FCSTD DOCUMENT  (FreeCAD 1.0R39319 (Git))
Label: Assembly_PSU-Stack
License: All rights reserved
LicenseURL: https://en.wikipedia.org/wiki/All_rights_reserved
objects: App::FeaturePython×22, App::Link×11, Assembly::JointGroup×1, Assembly::AssemblyObject×1
EXTERNAL_REF file=../Part/Print/Stack_Module_PSU.FCStd obj=Part
EXTERNAL_REF file=../Part/Print/Ambient_LED_Screen.FCStd obj=Part
EXTERNAL_REF file=../Part/Print/LinePower_Cover.FCStd obj=Part
EXTERNAL_REF file=../Part/Print/Foot.FCStd obj=Part
EXTERNAL_REF file=../Part/Print/Spacer.FCStd obj=Part

FEATURE [App::Link] Stack_Module_PSU
  LinkedObject = -> <external ../Part/Print/Stack_Module_PSU.FCStd>#Part
FEATURE [App::FeaturePython] GroundedJoint  # Assembly grounded joint (typed FeaturePython)
  ObjectToGround = -> Stack_Module_PSU
FEATURE [App::Link] Ambient_LED_Screen
  LinkPlacement = pos=(-1.22e-14,-3,-62.5) rot=(0,0.707107,-0.707107;3.14159rad)
  LinkedObject = -> <external ../Part/Print/Ambient_LED_Screen.FCStd>#Part
  Placement = pos=(-1.22e-14,-3,-62.5) rot=(0,0.707107,-0.707107;3.14159rad)
FEATURE [App::FeaturePython] Joint  label="Distance"  # Assembly joint (typed FeaturePython)
  Activated = true
  AngleMax = 0
  AngleMin = 0
  Detach1 = false
  Detach2 = false
  Distance = 0
  Distance2 = 0
  EnableAngleMax = false
  EnableAngleMin = false
  EnableLengthMax = false
  EnableLengthMin = false
  JointType = 5 (Distance)
  LengthMax = 0
  LengthMin = 0
  Placement1 = pos=(5.02e-14,1.20274,-3.5e-15) rot=(0,1,0;3.14159rad)
  Placement2 = pos=(-3.81809,-3,-7.3136) rot=(1,0,0;1.5708rad)
  Reference1 = -> Assembly [Ambient_LED_Screen.Body.Face51,Ambient_LED_Screen.Body.Edge30]
  Reference2 = -> Assembly [Stack_Module_PSU.Body.Face1201,Stack_Module_PSU.Body.Edge768]
FEATURE [App::FeaturePython] Joint001  label="Cylindrical"  # Assembly joint (typed FeaturePython)
  Activated = true
  AngleMax = 0
  AngleMin = 0
  Detach1 = false
  Detach2 = false
  Distance = 0
  Distance2 = 0
  EnableAngleMax = false
  EnableAngleMin = false
  EnableLengthMax = false
  EnableLengthMin = false
  JointType = 2 (Cylindrical)
  LengthMax = 0
  LengthMin = 0
  Placement1 = pos=(60.5,3,0) rot=(1,0,0;3.14159rad)
  Placement2 = pos=(-60.5,1.29e-14,-65.5) rot=(0,0.707107,0.707107;3.14159rad)
  Reference1 = -> Assembly [Ambient_LED_Screen.Body.Face52,Ambient_LED_Screen.Body.Edge2]
  Reference2 = -> Assembly [Stack_Module_PSU.Body.Face1184,Stack_Module_PSU.Body.Edge3]
FEATURE [App::FeaturePython] Joint002  label="Cylindrical001"  # Assembly joint (typed FeaturePython)
  Activated = true
  AngleMax = 0
  AngleMin = 0
  Detach1 = false
  Detach2 = false
  Distance = 0
  Distance2 = 0
  EnableAngleMax = false
  EnableAngleMin = false
  EnableLengthMax = false
  EnableLengthMin = false
  JointType = 2 (Cylindrical)
  LengthMax = 0
  LengthMin = 0
  Placement1 = pos=(-60.5,3,-1.34e-14) rot=(0,0,1;3.14159rad)
  Placement2 = pos=(60.5,-1.5,-65.5) rot=(1,0,0;1.5708rad)
  Reference1 = -> Assembly [Ambient_LED_Screen.Body.Face54,Ambient_LED_Screen.Body.Edge2]
  Reference2 = -> Assembly [Stack_Module_PSU.Body.Face1185,Stack_Module_PSU.Body.Face1185]
FEATURE [App::Link] LinePower_Cover
  LinkPlacement = pos=(56,-4,67) rot=(0,-0.707107,0.707107;3.14159rad)
  LinkedObject = -> <external ../Part/Print/LinePower_Cover.FCStd>#Part
  Placement = pos=(56,-4,67) rot=(0,-0.707107,0.707107;3.14159rad)
FEATURE [App::FeaturePython] Joint003  label="Distance001"  # Assembly joint (typed FeaturePython)
  Activated = true
  AngleMax = 0
  AngleMin = 0
  Detach1 = false
  Detach2 = false
  Distance = 0
  Distance2 = 0
  EnableAngleMax = false
  EnableAngleMin = false
  EnableLengthMax = false
  EnableLengthMin = false
  JointType = 5 (Distance)
  LengthMax = 0
  LengthMin = 0
  Placement1 = pos=(42.2837,4.81718,4) rot=(0,0,1;0rad)
  Placement2 = pos=(12.8084,-8,63.1916) rot=(0.57735,0.57735,0.57735;4.18879rad)
  Reference1 = -> Assembly [LinePower_Cover.Body.Face19,LinePower_Cover.Body.Face19]
  Reference2 = -> Assembly [Stack_Module_PSU.Body.Face1235,Stack_Module_PSU.Body.Edge6]
FEATURE [App::FeaturePython] Joint004  label="Cylindrical002"  # Assembly joint (typed FeaturePython)
  Activated = true
  AngleMax = 0
  AngleMin = 0
  Detach1 = false
  Detach2 = false
  Distance = 0
  Distance2 = 0
  EnableAngleMax = false
  EnableAngleMin = false
  EnableLengthMax = false
  EnableLengthMin = false
  JointType = 2 (Cylindrical)
  LengthMax = 0
  LengthMin = 0
  Placement1 = pos=(43,4,5) rot=(0,0,1;0rad)
  Placement2 = pos=(13,-5.5,63) rot=(1,0,0;1.5708rad)
  Reference1 = -> Assembly [LinePower_Cover.Body.Face35,LinePower_Cover.Body.Face35]
  Reference2 = -> Assembly [Stack_Module_PSU.Body.Face1271,Stack_Module_PSU.Body.Face1271]
FEATURE [App::FeaturePython] Joint005  label="Cylindrical003"  # Assembly joint (typed FeaturePython)
  Activated = true
  AngleMax = 0
  AngleMin = 0
  Detach1 = false
  Detach2 = false
  Distance = 0
  Distance2 = 0
  EnableAngleMax = false
  EnableAngleMin = false
  EnableLengthMax = false
  EnableLengthMin = false
  JointType = 2 (Cylindrical)
  LengthMax = 0
  LengthMin = 0
  Placement1 = pos=(3,36,5) rot=(0,0,1;0rad)
  Placement2 = pos=(53,-5.5,31) rot=(1,0,0;1.5708rad)
  Reference1 = -> Assembly [LinePower_Cover.Body.Face36,LinePower_Cover.Body.Face36]
  Reference2 = -> Assembly [Stack_Module_PSU.Body.Face1265,Stack_Module_PSU.Body.Face1265]
FEATURE [App::Link] Foot
  LinkPlacement = pos=(-66.5,5,-53.5) rot=(0.57735,-0.57735,0.57735;2.0944rad)
  LinkedObject = -> <external ../Part/Print/Foot.FCStd>#Part
  Placement = pos=(-66.5,5,-53.5) rot=(0.57735,-0.57735,0.57735;2.0944rad)
FEATURE [App::Link] Foot001
  LinkPlacement = pos=(-63.5,5,62.5) rot=(0.57735,-0.57735,0.57735;2.0944rad)
  LinkedObject = -> <external ../Part/Print/Foot.FCStd>#Part
  Placement = pos=(-63.5,5,62.5) rot=(0.57735,-0.57735,0.57735;2.0944rad)
FEATURE [App::Link] Foot002
  LinkPlacement = pos=(66.5,5,-53.5) rot=(1,0,0;1.5708rad)
  LinkedObject = -> <external ../Part/Print/Foot.FCStd>#Part
  Placement = pos=(66.5,5,-53.5) rot=(1,0,0;1.5708rad)
FEATURE [App::Link] Foot003
  LinkPlacement = pos=(63.5,5,62.5) rot=(0.57735,-0.57735,0.57735;2.0944rad)
  LinkedObject = -> <external ../Part/Print/Foot.FCStd>#Part
  Placement = pos=(63.5,5,62.5) rot=(0.57735,-0.57735,0.57735;2.0944rad)
FEATURE [App::FeaturePython] Joint006  label="Cylindrical004"  # Assembly joint (typed FeaturePython)
  Activated = true
  AngleMax = 0
  AngleMin = 0
  Detach1 = false
  Detach2 = false
  Distance = 0
  Distance2 = 0
  EnableAngleMax = false
  EnableAngleMin = false
  EnableLengthMax = false
  EnableLengthMin = false
  JointType = 2 (Cylindrical)
  LengthMax = 0
  LengthMin = 0
  Placement1 = pos=(0,4e-16,2) rot=(1,0,0;3.14159rad)
  Placement2 = pos=(66.5,-2.5,-53.5) rot=(-1,0,0;1.5708rad)
  Reference1 = -> Assembly [Foot002.Body.Face12,Foot002.Body.Face12]
  Reference2 = -> Assembly [Stack_Module_PSU.Body.Face83,Stack_Module_PSU.Body.Face83]
FEATURE [App::FeaturePython] Joint007  label="Distance002"  # Assembly joint (typed FeaturePython)
  Activated = true
  AngleMax = 0
  AngleMin = 0
  Detach1 = false
  Detach2 = false
  Distance = 0
  Distance2 = 0
  EnableAngleMax = false
  EnableAngleMin = false
  EnableLengthMax = false
  EnableLengthMin = false
  JointType = 5 (Distance)
  LengthMax = 0
  LengthMin = 0
  Placement1 = pos=(9e-16,2.4e-15,5) rot=(0,0,1;3.14159rad)
  Placement2 = pos=(1.08804,3.9e-15,3.01175) rot=(-0.57735,0.57735,0.57735;2.0944rad)
  Reference1 = -> Assembly [Foot002.Body.Face3,Foot002.Body.Face3]
  Reference2 = -> Assembly [Stack_Module_PSU.Body.Face7,Stack_Module_PSU.Body.Vertex102]
FEATURE [App::FeaturePython] Joint008  label="Distance003"  # Assembly joint (typed FeaturePython)
  Activated = true
  AngleMax = 0
  AngleMin = 0
  Detach1 = false
  Detach2 = false
  Distance = 0
  Distance2 = 0
  EnableAngleMax = false
  EnableAngleMin = false
  EnableLengthMax = false
  EnableLengthMin = false
  JointType = 5 (Distance)
  LengthMax = 0
  LengthMin = 0
  Placement1 = pos=(9e-16,2.4e-15,5) rot=(0,0,1;3.14159rad)
  Placement2 = pos=(1.08804,3.9e-15,3.01175) rot=(-0.57735,0.57735,0.57735;2.0944rad)
  Reference1 = -> Assembly [Foot003.Body.Face3,Foot003.Body.Face3]
  Reference2 = -> Assembly [Stack_Module_PSU.Body.Face7,Stack_Module_PSU.Body.Vertex92]
FEATURE [App::FeaturePython] Joint009  label="Cylindrical005"  # Assembly joint (typed FeaturePython)
  Activated = true
  AngleMax = 0
  AngleMin = 0
  Detach1 = false
  Detach2 = false
  Distance = 0
  Distance2 = 0
  EnableAngleMax = false
  EnableAngleMin = false
  EnableLengthMax = false
  EnableLengthMin = false
  JointType = 2 (Cylindrical)
  LengthMax = 0
  LengthMin = 0
  Placement1 = pos=(0,4e-16,2) rot=(1,0,0;3.14159rad)
  Placement2 = pos=(63.5,-2.5,62.5) rot=(-1,0,0;1.5708rad)
  Reference1 = -> Assembly [Foot003.Body.Face12,Foot003.Body.Face12]
  Reference2 = -> Assembly [Stack_Module_PSU.Body.Face82,Stack_Module_PSU.Body.Face82]
FEATURE [App::FeaturePython] Joint010  label="Distance004"  # Assembly joint (typed FeaturePython)
  Activated = true
  AngleMax = 0
  AngleMin = 0
  Detach1 = false
  Detach2 = false
  Distance = 0
  Distance2 = 0
  EnableAngleMax = false
  EnableAngleMin = false
  EnableLengthMax = false
  EnableLengthMin = false
  JointType = 5 (Distance)
  LengthMax = 0
  LengthMin = 0
  Placement1 = pos=(9e-16,2.4e-15,5) rot=(0,0,1;3.14159rad)
  Placement2 = pos=(1.08804,3.9e-15,3.01175) rot=(-0.57735,0.57735,0.57735;2.0944rad)
  Reference1 = -> Assembly [Foot001.Body.Face3,Foot001.Body.Face3]
  Reference2 = -> Assembly [Stack_Module_PSU.Body.Face7,Stack_Module_PSU.Body.Vertex89]
FEATURE [App::FeaturePython] Joint011  label="Cylindrical006"  # Assembly joint (typed FeaturePython)
  Activated = true
  AngleMax = 0
  AngleMin = 0
  Detach1 = false
  Detach2 = false
  Distance = 0
  Distance2 = 0
  EnableAngleMax = false
  EnableAngleMin = false
  EnableLengthMax = false
  EnableLengthMin = false
  JointType = 2 (Cylindrical)
  LengthMax = 0
  LengthMin = 0
  Placement1 = pos=(0,4e-16,2) rot=(1,0,0;3.14159rad)
  Placement2 = pos=(-63.5,-2.5,62.5) rot=(0,0.707107,-0.707107;3.14159rad)
  Reference1 = -> Assembly [Foot001.Body.Face12,Foot001.Body.Face12]
  Reference2 = -> Assembly [Stack_Module_PSU.Body.Face80,Stack_Module_PSU.Body.Face80]
FEATURE [App::FeaturePython] Joint012  label="Distance005"  # Assembly joint (typed FeaturePython)
  Activated = true
  AngleMax = 0
  AngleMin = 0
  Detach1 = false
  Detach2 = false
  Distance = 0
  Distance2 = 0
  EnableAngleMax = false
  EnableAngleMin = false
  EnableLengthMax = false
  EnableLengthMin = false
  JointType = 5 (Distance)
  LengthMax = 0
  LengthMin = 0
  Placement1 = pos=(9e-16,2.4e-15,5) rot=(0,0,1;3.14159rad)
  Placement2 = pos=(1.08804,3.9e-15,3.01175) rot=(-0.57735,0.57735,0.57735;2.0944rad)
  Reference1 = -> Assembly [Foot.Body.Face3,Foot.Body.Face3]
  Reference2 = -> Assembly [Stack_Module_PSU.Body.Face7,Stack_Module_PSU.Body.Edge11]
FEATURE [App::FeaturePython] Joint013  label="Cylindrical007"  # Assembly joint (typed FeaturePython)
  Activated = true
  AngleMax = 0
  AngleMin = 0
  Detach1 = false
  Detach2 = false
  Distance = 0
  Distance2 = 0
  EnableAngleMax = false
  EnableAngleMin = false
  EnableLengthMax = false
  EnableLengthMin = false
  JointType = 2 (Cylindrical)
  LengthMax = 0
  LengthMin = 0
  Placement1 = pos=(0,4e-16,2) rot=(1,0,0;3.14159rad)
  Placement2 = pos=(-66.5,-2.5,-53.5) rot=(0,0.707107,-0.707107;3.14159rad)
  Reference1 = -> Assembly [Foot.Body.Face12,Foot.Body.Face12]
  Reference2 = -> Assembly [Stack_Module_PSU.Body.Face81,Stack_Module_PSU.Body.Face81]
FEATURE [App::Link] Spacer
  LinkPlacement = pos=(66.5,-35.25,-53.5) rot=(-0.57735,0.57735,-0.57735;4.18879rad)
  LinkedObject = -> <external ../Part/Print/Spacer.FCStd>#Part
  Placement = pos=(66.5,-35.25,-53.5) rot=(-0.57735,0.57735,-0.57735;4.18879rad)
FEATURE [App::Link] Spacer001
  LinkPlacement = pos=(63.5,-35.25,62.5) rot=(-0.57735,0.57735,-0.57735;4.18879rad)
  LinkedObject = -> <external ../Part/Print/Spacer.FCStd>#Part
  Placement = pos=(63.5,-35.25,62.5) rot=(-0.57735,0.57735,-0.57735;4.18879rad)
FEATURE [App::Link] Spacer002
  LinkPlacement = pos=(-66.5,-35.25,-53.5) rot=(-0.57735,0.57735,-0.57735;4.18879rad)
  LinkedObject = -> <external ../Part/Print/Spacer.FCStd>#Part
  Placement = pos=(-66.5,-35.25,-53.5) rot=(-0.57735,0.57735,-0.57735;4.18879rad)
FEATURE [App::Link] Spacer003
  LinkPlacement = pos=(-63.5,-35.25,62.5) rot=(0.57735,-0.57735,0.57735;2.0944rad)
  LinkedObject = -> <external ../Part/Print/Spacer.FCStd>#Part
  Placement = pos=(-63.5,-35.25,62.5) rot=(0.57735,-0.57735,0.57735;2.0944rad)
FEATURE [App::FeaturePython] Joint014  label="Distance006"  # Assembly joint (typed FeaturePython)
  Activated = true
  AngleMax = 0
  AngleMin = 0
  Detach1 = false
  Detach2 = false
  Distance = 0
  Distance2 = 0
  EnableAngleMax = false
  EnableAngleMin = false
  EnableLengthMax = false
  EnableLengthMin = false
  JointType = 5 (Distance)
  LengthMax = 0
  LengthMin = 0
  Placement1 = pos=(-3.1e-15,-9e-16,0) rot=(0,0,1;0rad)
  Placement2 = pos=(66.5,-35.25,-53.5) rot=(0.57735,0.57735,0.57735;4.18879rad)
  Reference1 = -> Assembly [Spacer.Body.Face4,Spacer.Body.Face4]
  Reference2 = -> Assembly [Stack_Module_PSU.Body.Face1241,Stack_Module_PSU.Body.Face1241]
FEATURE [App::FeaturePython] Joint015  label="Cylindrical008"  # Assembly joint (typed FeaturePython)
  Activated = true
  AngleMax = 0
  AngleMin = 0
  Detach1 = false
  Detach2 = false
  Distance = 0
  Distance2 = 0
  EnableAngleMax = false
  EnableAngleMin = false
  EnableLengthMax = false
  EnableLengthMin = false
  JointType = 2 (Cylindrical)
  LengthMax = 0
  LengthMin = 0
  Placement1 = pos=(0,0,3.5) rot=(0,0,1;0rad)
  Placement2 = pos=(66.5,-37.75,-53.5) rot=(1,0,0;1.5708rad)
  Reference1 = -> Assembly [Spacer.Body.Face1,Spacer.Body.Face1]
  Reference2 = -> Assembly [Stack_Module_PSU.Body.Face71,Stack_Module_PSU.Body.Face71]
FEATURE [App::FeaturePython] Joint016  label="Distance007"  # Assembly joint (typed FeaturePython)
  Activated = true
  AngleMax = 0
  AngleMin = 0
  Detach1 = false
  Detach2 = false
  Distance = 0
  Distance2 = 0
  EnableAngleMax = false
  EnableAngleMin = false
  EnableLengthMax = false
  EnableLengthMin = false
  JointType = 5 (Distance)
  LengthMax = 0
  LengthMin = 0
  Placement1 = pos=(-3.1e-15,-9e-16,0) rot=(0,0,1;0rad)
  Placement2 = pos=(63.5,-35.25,62.5) rot=(0.57735,0.57735,0.57735;4.18879rad)
  Reference1 = -> Assembly [Spacer001.Body.Face4,Spacer001.Body.Face4]
  Reference2 = -> Assembly [Stack_Module_PSU.Body.Face1240,Stack_Module_PSU.Body.Edge2]
FEATURE [App::FeaturePython] Joint017  label="Distance008"  # Assembly joint (typed FeaturePython)
  Activated = true
  AngleMax = 0
  AngleMin = 0
  Detach1 = false
  Detach2 = false
  Distance = 0
  Distance2 = 0
  EnableAngleMax = false
  EnableAngleMin = false
  EnableLengthMax = false
  EnableLengthMin = false
  JointType = 5 (Distance)
  LengthMax = 0
  LengthMin = 0
  Placement1 = pos=(-3.1e-15,-9e-16,0) rot=(0,0,1;0rad)
  Placement2 = pos=(-66.5,-35.25,-53.5) rot=(0.57735,-0.57735,0.57735;2.0944rad)
  Reference1 = -> Assembly [Spacer002.Body.Face4,Spacer002.Body.Vertex5]
  Reference2 = -> Assembly [Stack_Module_PSU.Body.Face1239,Stack_Module_PSU.Body.Vertex2511]
FEATURE [App::FeaturePython] Joint018  label="Cylindrical009"  # Assembly joint (typed FeaturePython)
  Activated = true
  AngleMax = 0
  AngleMin = 0
  Detach1 = false
  Detach2 = false
  Distance = 0
  Distance2 = 0
  EnableAngleMax = false
  EnableAngleMin = false
  EnableLengthMax = false
  EnableLengthMin = false
  JointType = 2 (Cylindrical)
  LengthMax = 0
  LengthMin = 0
  Placement1 = pos=(0,0,3.5) rot=(0,0,1;0rad)
  Placement2 = pos=(-66.5,-37.75,-53.5) rot=(0,0.707107,0.707107;3.14159rad)
  Reference1 = -> Assembly [Spacer002.Body.Face1,Spacer002.Body.Face1]
  Reference2 = -> Assembly [Stack_Module_PSU.Body.Face69,Stack_Module_PSU.Body.Face69]
FEATURE [App::FeaturePython] Joint019  label="Distance009"  # Assembly joint (typed FeaturePython)
  Activated = true
  AngleMax = 0
  AngleMin = 0
  Detach1 = false
  Detach2 = false
  Distance = 0
  Distance2 = 0
  EnableAngleMax = false
  EnableAngleMin = false
  EnableLengthMax = false
  EnableLengthMin = false
  JointType = 5 (Distance)
  LengthMax = 0
  LengthMin = 0
  Placement1 = pos=(-3.1e-15,-9e-16,0) rot=(0,0,1;0rad)
  Placement2 = pos=(-63.5,-35.25,62.5) rot=(0.57735,-0.57735,0.57735;2.0944rad)
  Reference1 = -> Assembly [Spacer003.Body.Face4,Spacer003.Body.Vertex5]
  Reference2 = -> Assembly [Stack_Module_PSU.Body.Face1238,Stack_Module_PSU.Body.Vertex2510]
FEATURE [App::FeaturePython] Joint020  label="Cylindrical010"  # Assembly joint (typed FeaturePython)
  Activated = true
  AngleMax = 0
  AngleMin = 0
  Detach1 = false
  Detach2 = false
  Distance = 0
  Distance2 = 0
  EnableAngleMax = false
  EnableAngleMin = false
  EnableLengthMax = false
  EnableLengthMin = false
  JointType = 2 (Cylindrical)
  LengthMax = 0
  LengthMin = 0
  Placement1 = pos=(0,0,3.5) rot=(0,0,1;0rad)
  Placement2 = pos=(-63.5,-37.75,62.5) rot=(0,0.707107,0.707107;3.14159rad)
  Reference1 = -> Assembly [Spacer003.Body.Face1,Spacer003.Body.Face1]
  Reference2 = -> Assembly [Stack_Module_PSU.Body.Face68,Stack_Module_PSU.Body.Face68]
FEATURE [Assembly::JointGroup] Joints
  Group = -> [GroundedJoint,Joint,Joint001,Joint002,Joint003,Joint004,Joint005,Joint006,Joint007,Joint008,Joint009,Joint010,Joint011,Joint012,Joint013,Joint014,Joint015,Joint016,Joint017,Joint018,Joint019,Joint020]
FEATURE [Assembly::AssemblyObject] Assembly  label="Assembly_PSU-Stack"
  Group = -> [Joints,Stack_Module_PSU,GroundedJoint,Ambient_LED_Screen,Joint,Joint001,Joint002,LinePower_Cover,Joint003,Joint004,Joint005,Foot,Foot001,Foot002,Foot003,Joint006,Joint007,Joint008,Joint009,Joint010,Joint011,Joint012,Joint013,Spacer,Spacer001,Spacer002,Spacer003,Joint014,Joint015,Joint016,Joint017,Joint018,Joint019,Joint020]
  Origin = -> Origin
  Type = Assembly

RESOLVED EXTERNAL PARTS (link-assembly join: the EXTERNAL_REF files above that resolve inside this repo's crawl, each included once):
---- part ../Part/Print/Ambient_LED_Screen.FCStd = doc fcstd_3e985b0e07c3 ----
FCSTD DOCUMENT  (FreeCAD 1.0R39319 (Git))
Label: Ambient_LED_Screen
License: All rights reserved
LicenseURL: https://en.wikipedia.org/wiki/All_rights_reserved
objects: Sketcher::SketchObject×7, PartDesign::Pocket×5, PartDesign::Pad×2, PartDesign::Chamfer×1, PartDesign::Mirrored×1, PartDesign::Body×1, PartDesign::CoordinateSystem×1, App::Part×1
note: 42 computed .brp shape members not serialized (recipe doc carries the construction recipe); baked Part::Feature solids carry a one-line shape summary decoded from their .brp

FEATURE [Sketcher::SketchObject] Sketch
  ArcFitTolerance = 1e-06
  AttachmentSupport = -> [XY_Plane001]
  FullyConstrained = true
  MakeInternals = false
  MapMode = 5
  sketch-geometry (20):
    g0: LineSegment StartX=52.3059 StartY=0 StartZ=0 EndX=60.5 EndY=0 EndZ=0
    g1: ArcOfCircle CenterX=60.5 CenterY=3 CenterZ=0 NormalX=0 NormalY=0 NormalZ=1 AngleXU=0 Radius=3 StartAngle=4.71239 EndAngle=8.29889
    g2: LineSegment StartX=59.2089 StartY=5.70795 StartZ=0 EndX=48.6478 EndY=0.672534 EndZ=0
    g3: ArcOfCircle CenterX=0 CenterY=4.259 CenterZ=0 NormalX=0 NormalY=0 NormalZ=1 AngleXU=0 Radius=7 StartAngle=4.71239 EndAngle=5.61581
    g4: ArcOfCircle CenterX=0 CenterY=4.259 CenterZ=0 NormalX=0 NormalY=0 NormalZ=1 AngleXU=0 Radius=5.5 StartAngle=4.71239 EndAngle=5.61581
    g5: LineSegment StartX=-1.3e-15 StartY=-2.741 StartZ=0 EndX=-1.3e-15 EndY=-1.241 EndZ=0
    g6: ArcOfCircle CenterX=10.9963 CenterY=-4.40596 CenterZ=0 NormalX=0 NormalY=0 NormalZ=1 AngleXU=0 Radius=7 StartAngle=0.667374 EndAngle=2.47422
    g7: ArcOfCircle CenterX=10.9963 CenterY=-4.40596 CenterZ=0 NormalX=0 NormalY=0 NormalZ=1 AngleXU=0 Radius=8.5 StartAngle=0.667374 EndAngle=2.47422
    g8: ArcOfCircle CenterX=21.9926 CenterY=4.259 CenterZ=0 NormalX=0 NormalY=0 NormalZ=1 AngleXU=0 Radius=5.5 StartAngle=3.80897 EndAngle=5.61581
    g9: ArcOfCircle CenterX=21.9926 CenterY=4.259 CenterZ=0 NormalX=0 NormalY=0 NormalZ=1 AngleXU=0 Radius=7 StartAngle=3.80897 EndAngle=5.61581
    g10: ArcOfCircle CenterX=32.9889 CenterY=-4.40596 CenterZ=0 NormalX=0 NormalY=0 NormalZ=1 AngleXU=0 Radius=8.5 StartAngle=0.667374 EndAngle=2.47422
    g11: ArcOfCircle CenterX=32.9889 CenterY=-4.40596 CenterZ=0 NormalX=0 NormalY=0 NormalZ=1 AngleXU=0 Radius=7 StartAngle=0.667374 EndAngle=2.47422
    g12: ArcOfCircle CenterX=43.9852 CenterY=4.259 CenterZ=0 NormalX=0 NormalY=0 NormalZ=1 AngleXU=0 Radius=7 StartAngle=3.80897 EndAngle=5.34883
    g13: ArcOfCircle CenterX=43.9852 CenterY=4.259 CenterZ=0 NormalX=0 NormalY=0 NormalZ=1 AngleXU=0 Radius=5.5 StartAngle=3.80897 EndAngle=5.34883
    g14: ArcOfCircle CenterX=52.3059 CenterY=-7 CenterZ=0 NormalX=0 NormalY=0 NormalZ=1 AngleXU=0 Radius=8.5 StartAngle=2.0157 EndAngle=2.20724
    g15: ArcOfCircle CenterX=52.3059 CenterY=-7 CenterZ=0 NormalX=0 NormalY=0 NormalZ=1 AngleXU=0 Radius=7 StartAngle=1.5708 EndAngle=2.20724
    g16: GeomPoint [constr] X=66 Y=10 Z=0
    g17: LineSegment [constr] StartX=48.1455 StartY=-1.3705 StartZ=0 EndX=50 EndY=2e-16 EndZ=0
    g18: LineSegment [constr] StartX=10.9963 StartY=-4.40596 StartZ=0 EndX=32.9889 EndY=-4.40596 EndZ=0
    g19: LineSegment [constr] StartX=0 StartY=4.259 StartZ=0 EndX=43.9852 EndY=4.259 EndZ=0
  constraints (49):
    c: PointOnObject(g0,g-1)
    c: PointOnObject(g0,g-1)
    c: Tangent(g0,g1) = -1.5708
    c: Tangent(g1,g2) = -1.5708
    c: Coincident(g5,g3)
    c: Coincident(g5,g4)
    c: Vertical(g5)
    c: Coincident(g4,g3)
    c: PointOnObject(g3,g-2)
    c: Tangent(g6,g3) = 1.5708
    c: Tangent(g7,g4) = 1.5708
    c: Coincident(g6,g7)
    c: Radius(g6) = 7
    c: Distance(g5,g5) = 1.5
    c: Tangent(g8,g7) = 1.5708
    c: Tangent(g9,g6) = 1.5708
    c: Coincident(g9,g8)
    c: PointOnObject(g3,g-2)
    c: Tangent(g10,g8) = 1.5708
    c: Tangent(g11,g9) = 1.5708
    c: Coincident(g11,g10)
    c: Tangent(g12,g11) = 1.5708
    c: Tangent(g13,g10) = 1.5708
    c: Coincident(g12,g13)
    c: Tangent(g14,g13) = 1.5708
    c: Tangent(g14,g2) = -1.5708
    c: Tangent(g15,g0) = 1.5708
    c: Radius(g9) = 7
    c: Radius(g12) = 7
    c: Coincident(g15,g14)
    c: DistanceX(g-1,g16) = 66
    c: Distance(g16,g-1) = 10
    c: Radius(g1) = 3
    c: Distance(g1,g-2) = 60.5
    c: Tangent(g15,g12) = 1.5708
    c: Tangent(g12,g17) = -1.5708
    c: Radius(g3) = 7
    c: Radius(g11) = 7
    c: Radius(g15) = 7
    c: PointOnObject(g17,g-1)
    c: DistanceX(g-1,g17) = 50
    c: Coincident(g18,g6)
    c: Coincident(g18,g10)
    c: Coincident(g19,g3)
    c: Coincident(g19,g12)
    c: Horizontal(g19)
    c: PointOnObject(g8,g19)
    c: Horizontal(g18)
    c: Distance(g-1,g19) = 4.259
FEATURE [PartDesign::Pad] Pad
  Direction = (0,0,1)
  Length = 34.25
  Length2 = 10
  Profile = -> Sketch
  ReferenceAxis = -> Sketch [N_Axis]
  Refine = true
  Suppressed = false
  Type = 0
FEATURE [Sketcher::SketchObject] Sketch001
  ArcFitTolerance = 1e-06
  AttachmentSupport = -> [Pad]
  ExternalGeometry = -> [Pad]
  FullyConstrained = true
  MakeInternals = false
  MapMode = 5
  Placement = pos=(0,0,0) rot=(1,0,0;3.14159rad)
  sketch-geometry (1):
    g0: Circle CenterX=60.5 CenterY=-3 CenterZ=0 NormalX=0 NormalY=0 NormalZ=1 AngleXU=0 Radius=1.25
  constraints (2):
    c: Coincident(g0,g-3)
    c: Diameter(g0) = 2.5
FEATURE [PartDesign::Pocket] Pocket
  BaseFeature = -> Pad
  Direction = (0,0,1)
  Length = 10
  Length2 = 5
  Profile = -> Sketch001
  ReferenceAxis = -> Sketch001 [N_Axis]
  Refine = true
  Suppressed = false
  Type = 0
FEATURE [Sketcher::SketchObject] Sketch002
  ArcFitTolerance = 1e-06
  AttachmentSupport = -> [Pocket]
  FullyConstrained = true
  MakeInternals = false
  MapMode = 5
  Placement = pos=(0,0,34.25) rot=(0,0,1;0rad)
  sketch-geometry (4):
    g0: LineSegment StartX=0 StartY=7.59 StartZ=0 EndX=0 EndY=-5.3 EndZ=0
    g1: LineSegment StartX=0 StartY=-5.3 StartZ=0 EndX=70.5 EndY=-5.3 EndZ=0
    g2: LineSegment StartX=70.5 StartY=-5.3 StartZ=0 EndX=70.5 EndY=7.59 EndZ=0
    g3: LineSegment StartX=70.5 StartY=7.59 StartZ=0 EndX=0 EndY=7.59 EndZ=0
  constraints (12):
    c: Coincident(g0,g1)
    c: Coincident(g1,g2)
    c: Coincident(g2,g3)
    c: Coincident(g3,g0)
    c: Vertical(g0)
    c: Vertical(g2)
    c: Horizontal(g1)
    c: Horizontal(g3)
    c: PointOnObject(g0,g-2)
    c: Distance(g2,g0) = 70.5
    c: Distance(g3,g1) = 12.89
    c: Distance(g1,g-1) = 5.3
FEATURE [PartDesign::Pad] Pad001
  BaseFeature = -> Pocket
  Direction = (0,0,1)
  Length = 3
  Length2 = 10
  Profile = -> Sketch002
  ReferenceAxis = -> Sketch002 [N_Axis]
  Refine = true
  Suppressed = false
  Type = 0
FEATURE [Sketcher::SketchObject] Sketch003
  ArcFitTolerance = 1e-06
  AttachmentSupport = -> [Pad001]
  ExternalGeometry = -> [Pad001]
  FullyConstrained = true
  MakeInternals = false
  MapMode = 5
  Placement = pos=(0,0,37.25) rot=(0,0,1;0rad)
  sketch-geometry (4):
    g0: LineSegment StartX=70.5 StartY=-2.5 StartZ=0 EndX=55.5 EndY=-2.5 EndZ=0
    g1: LineSegment StartX=55.5 StartY=-2.5 StartZ=0 EndX=55.5 EndY=-5.3 EndZ=0
    g2: LineSegment StartX=55.5 StartY=-5.3 StartZ=0 EndX=70.5 EndY=-5.3 EndZ=0
    g3: LineSegment StartX=70.5 StartY=-5.3 StartZ=0 EndX=70.5 EndY=-2.5 EndZ=0
  constraints (12):
    c: Coincident(g0,g1)
    c: Coincident(g1,g2)
    c: Coincident(g2,g3)
    c: Coincident(g3,g0)
    c: Horizontal(g0)
    c: Horizontal(g2)
    c: Vertical(g1)
    c: Vertical(g3)
    c: PointOnObject(g0,g-3)
    c: PointOnObject(g1,g-4)
    c: Distance(g3,g1) = 15
    c: Distance(g2,g0) = 2.8
FEATURE [PartDesign::Pocket] Pocket001
  BaseFeature = -> Pad001
  Direction = (0,0,-1)
  Length = 5
  Length2 = 5
  Profile = -> Sketch003
  ReferenceAxis = -> Sketch003 [N_Axis]
  Refine = true
  Suppressed = false
  Type = 1
FEATURE [Sketcher::SketchObject] Sketch004
  ArcFitTolerance = 1e-06
  AttachmentSupport = -> [Pocket001]
  ExternalGeometry = -> [Pocket001]
  FullyConstrained = true
  MakeInternals = false
  MapMode = 5
  Placement = pos=(0,0,37.25) rot=(0,0,1;0rad)
  sketch-geometry (4):
    g0: LineSegment StartX=65.5 StartY=7.59 StartZ=0 EndX=65.5 EndY=4.09 EndZ=0
    g1: LineSegment StartX=65.5 StartY=4.09 StartZ=0 EndX=70.5 EndY=4.09 EndZ=0
    g2: LineSegment StartX=70.5 StartY=4.09 StartZ=0 EndX=70.5 EndY=7.59 EndZ=0
    g3: LineSegment StartX=70.5 StartY=7.59 StartZ=0 EndX=65.5 EndY=7.59 EndZ=0
  constraints (12):
    c: Coincident(g0,g1)
    c: Coincident(g1,g2)
    c: Coincident(g2,g3)
    c: Coincident(g3,g0)
    c: Vertical(g0)
    c: Vertical(g2)
    c: Horizontal(g1)
    c: Horizontal(g3)
    c: PointOnObject(g0,g-4)
    c: Distance(g2,g0) = 5
    c: Distance(g1,g3) = 3.5
    c: PointOnObject(g1,g-3)
FEATURE [PartDesign::Pocket] Pocket002
  BaseFeature = -> Pocket001
  Direction = (0,0,-1)
  Length = 5
  Length2 = 5
  Profile = -> Sketch004
  ReferenceAxis = -> Sketch004 [N_Axis]
  Refine = true
  Suppressed = false
  Type = 1
FEATURE [Sketcher::SketchObject] Sketch005
  ArcFitTolerance = 1e-06
  AttachmentSupport = -> [Pocket002]
  ExternalGeometry = -> [Pocket002]
  FullyConstrained = true
  MakeInternals = false
  MapMode = 5
  Placement = pos=(0,0,37.25) rot=(0,0,1;0rad)
  sketch-geometry (1):
    g0: Circle CenterX=68 CenterY=1 CenterZ=0 NormalX=0 NormalY=0 NormalZ=1 AngleXU=0 Radius=1.5
  constraints (3):
    c: Distance(g0,g-2) = 68
    c: Distance(g0,g-3) = 3.5
    c: Diameter(g0) = 3
FEATURE [PartDesign::Pocket] Pocket003
  BaseFeature = -> Pocket002
  Direction = (0,0,-1)
  Length = 5
  Length2 = 5
  Profile = -> Sketch005
  ReferenceAxis = -> Sketch005 [N_Axis]
  Refine = true
  Suppressed = false
  Type = 1
FEATURE [Sketcher::SketchObject] Sketch006
  ArcFitTolerance = 1e-06
  AttachmentSupport = -> [Pocket003]
  ExternalGeometry = -> [Pocket003]
  FullyConstrained = true
  MakeInternals = false
  MapMode = 5
  Placement = pos=(0,0,37.25) rot=(0,0,1;0rad)
  sketch-geometry (2):
    g0: Circle CenterX=65.5 CenterY=4.09 CenterZ=0 NormalX=0 NormalY=0 NormalZ=1 AngleXU=0 Radius=0.5
    g1: Circle CenterX=55.5 CenterY=-2.5 CenterZ=0 NormalX=0 NormalY=0 NormalZ=1 AngleXU=0 Radius=0.5
  constraints (4):
    c: Coincident(g0,g-3)
    c: Coincident(g1,g-4)
    c: Diameter(g0) = 1
    c: Diameter(g1) = 1
FEATURE [PartDesign::Pocket] Pocket004
  BaseFeature = -> Pocket003
  Direction = (0,0,-1)
  Length = 5
  Length2 = 5
  Profile = -> Sketch006
  ReferenceAxis = -> Sketch006 [N_Axis]
  Refine = true
  Suppressed = false
  Type = 1
FEATURE [PartDesign::Chamfer] Chamfer
  Angle = 45
  Base = -> Pocket004 [Edge81,Edge68]
  BaseFeature = -> Pocket004
  ChamferType = 0
  FlipDirection = false
  Refine = true
  Size = 0.5
  Size2 = 1
  SupportTransform = false
  Suppressed = false
  UseAllEdges = false
FEATURE [PartDesign::Mirrored] Mirrored
  BaseFeature = -> Chamfer
  MirrorPlane = -> YZ_Plane001
  Refine = true
  Suppressed = false
  TransformMode = 1
FEATURE [PartDesign::Body] Body  label="Ambient_LED_Screen001"
  AllowCompound = false
  Group = -> [Sketch,Pad,Sketch001,Pocket,Sketch002,Pad001,Sketch003,Pocket001,Sketch004,Pocket002,Sketch005,Pocket003,Sketch006,Pocket004,Chamfer,Mirrored]
  Origin = -> Origin001
  Tip = -> Mirrored
FEATURE [PartDesign::CoordinateSystem] stack_att
  AttacherType = Attacher::AttachEngine3D
  AttachmentSupport = -> [Mirrored]
  MapMode = 11
  Placement = pos=(60.5,3,0) rot=(0.707107,-0.707107,0;3.14159rad)
FEATURE [App::Part] Part  label="Ambient_LED_Screen"
  Group = -> [Body,stack_att]
  Origin = -> Origin
---- part ../Part/Print/Foot.FCStd = doc fcstd_07f4133909bb ----
FCSTD DOCUMENT  (FreeCAD 1.0R39319 (Git))
Label: Foot
License: All rights reserved
LicenseURL: https://en.wikipedia.org/wiki/All_rights_reserved
objects: Sketcher::SketchObject×3, PartDesign::Pocket×2, PartDesign::CoordinateSystem×2, PartDesign::Revolution×1, PartDesign::Fillet×1, PartDesign::Chamfer×1, PartDesign::Body×1, App::Part×1
note: 24 computed .brp shape members not serialized (recipe doc carries the construction recipe); baked Part::Feature solids carry a one-line shape summary decoded from their .brp

FEATURE [Sketcher::SketchObject] Sketch
  ArcFitTolerance = 1e-06
  AttachmentSupport = -> [XZ_Plane001]
  FullyConstrained = true
  MakeInternals = false
  MapMode = 5
  Placement = pos=(0,0,0) rot=(1,0,0;1.5708rad)
  sketch-geometry (6):
    g0: LineSegment StartX=0 StartY=0 StartZ=0 EndX=0 EndY=9 EndZ=0
    g1: LineSegment StartX=0 StartY=9 StartZ=0 EndX=5.5 EndY=9 EndZ=0
    g2: LineSegment StartX=5.5 StartY=9 StartZ=0 EndX=5.5 EndY=5 EndZ=0
    g3: LineSegment StartX=5.5 StartY=5 StartZ=0 EndX=7.5 EndY=5 EndZ=0
    g4: LineSegment StartX=7.5 StartY=5 StartZ=0 EndX=7.5 EndY=0 EndZ=0
    g5: LineSegment StartX=7.5 StartY=0 StartZ=0 EndX=0 EndY=0 EndZ=0
  constraints (17):
    c: Coincident(g-1,g0)
    c: PointOnObject(g0,g-2)
    c: Coincident(g0,g1)
    c: Horizontal(g1)
    c: Coincident(g1,g2)
    c: Vertical(g2)
    c: Coincident(g2,g3)
    c: Horizontal(g3)
    c: Coincident(g3,g4)
    c: PointOnObject(g4,g-1)
    c: Vertical(g4)
    c: Coincident(g4,g5)
    c: Coincident(g5,g0)
    c: Distance(g5,g3) = 5
    c: Distance(g3,g1) = 4
    c: Distance(g4,g0) = 7.5
    c: Distance(g0,g2) = 5.5
FEATURE [PartDesign::Revolution] Revolution
  Angle = 360
  Angle2 = 60
  Axis = (0,2e-16,1)
  Base = (0,0,0)
  Placement = pos=(0,0,0) rot=(1,0,0;1.5708rad)
  Profile = -> Sketch
  ReferenceAxis = -> Sketch [V_Axis]
  Refine = true
  Reversed = true
  Suppressed = false
  Type = 0
FEATURE [Sketcher::SketchObject] Sketch001
  ArcFitTolerance = 1e-06
  AttachmentSupport = -> [Revolution]
  FullyConstrained = true
  MakeInternals = false
  MapMode = 5
  Placement = pos=(0,4e-15,9) rot=(0,0,1;3.14159rad)
  sketch-geometry (1):
    g0: Circle CenterX=0 CenterY=0 CenterZ=0 NormalX=0 NormalY=0 NormalZ=1 AngleXU=0 Radius=3
  constraints (2):
    c: Coincident(g0,g-1)
    c: Diameter(g0) = 6
FEATURE [PartDesign::Pocket] Pocket
  BaseFeature = -> Revolution
  Direction = (0,0,-1)
  Length = 5
  Length2 = 5
  Placement = pos=(0,0,0) rot=(1,0,0;1.5708rad)
  Profile = -> Sketch001
  ReferenceAxis = -> Sketch001 [N_Axis]
  Refine = true
  Suppressed = false
  Type = 1
FEATURE [Sketcher::SketchObject] Sketch002
  ArcFitTolerance = 1e-06
  AttachmentSupport = -> [Pocket]
  FullyConstrained = true
  MakeInternals = false
  MapMode = 5
  Placement = pos=(0,4e-15,9) rot=(0,0,1;3.14159rad)
  sketch-geometry (7):
    g0: LineSegment StartX=4.11362 StartY=2.375 StartZ=0 EndX=0 EndY=4.75 EndZ=0
    g1: LineSegment StartX=0 StartY=4.75 StartZ=0 EndX=-4.11362 EndY=2.375 EndZ=0
    g2: LineSegment StartX=-4.11362 StartY=2.375 StartZ=0 EndX=-4.11362 EndY=-2.375 EndZ=0
    g3: LineSegment StartX=-4.11362 StartY=-2.375 StartZ=0 EndX=-1.8e-15 EndY=-4.75 EndZ=0
    g4: LineSegment StartX=-1.5e-15 StartY=-4.75 StartZ=0 EndX=4.11362 EndY=-2.375 EndZ=0
    g5: LineSegment StartX=4.11362 StartY=-2.375 StartZ=0 EndX=4.11362 EndY=2.375 EndZ=0
    g6: Circle [constr] CenterX=0 CenterY=0 CenterZ=0 NormalX=0 NormalY=0 NormalZ=1 AngleXU=0 Radius=4.75
  constraints (16):
    c: Coincident(g0,g1)
    c: Coincident(g1,g2)
    c: Coincident(g2,g3)
    c: Coincident(g3,g4)
    c: Coincident(g4,g5)
    c: Coincident(g5,g0)
    c: Equal(g0, g1-g5) x5
    c: PointOnObject(g0,g6)
    c: PointOnObject(g1,g6)
    c: PointOnObject(g2,g6)
    c: PointOnObject(g3,g6)
    c: PointOnObject(g4,g6)
    c: PointOnObject(g5,g6)
    c: Coincident(g6,g-1)
    c: Diameter(g6) = 9.5
    c: PointOnObject(g0,g-2)
FEATURE [PartDesign::Pocket] Pocket001
  BaseFeature = -> Pocket
  Direction = (0,0,-1)
  Length = 5
  Length2 = 5
  Placement = pos=(0,0,0) rot=(1,0,0;1.5708rad)
  Profile = -> Sketch002
  ReferenceAxis = -> Sketch002 [N_Axis]
  Refine = true
  Suppressed = false
  Type = 0
FEATURE [PartDesign::Fillet] Fillet
  Base = -> Pocket001 [Edge22]
  BaseFeature = -> Pocket001
  Placement = pos=(0,0,0) rot=(1,0,0;1.5708rad)
  Radius = 1
  Refine = true
  SupportTransform = false
  Suppressed = false
  UseAllEdges = false
FEATURE [PartDesign::Chamfer] Chamfer
  Angle = 45
  Base = -> Fillet [Edge5]
  BaseFeature = -> Fillet
  ChamferType = 0
  FlipDirection = false
  Placement = pos=(0,0,0) rot=(1,0,0;1.5708rad)
  Refine = true
  Size = 0.5
  Size2 = 1
  SupportTransform = false
  Suppressed = false
  UseAllEdges = false
FEATURE [PartDesign::Body] Body  label="Foot001"
  AllowCompound = false
  Group = -> [Sketch,Revolution,Sketch001,Pocket,Sketch002,Pocket001,Fillet,Chamfer]
  Origin = -> Origin001
  Tip = -> Chamfer
FEATURE [PartDesign::CoordinateSystem] nut
  AttacherType = Attacher::AttachEngine3D
  AttachmentSupport = -> [Chamfer]
  MapMode = 11
  Placement = pos=(0,2.9e-15,4) rot=(0,0,-1;1.5708rad)
FEATURE [PartDesign::CoordinateSystem] base
  AttacherType = Attacher::AttachEngine3D
  AttachmentSupport = -> [Chamfer]
  MapMode = 11
  Placement = pos=(0,2e-15,0) rot=(0,0,-1;1.5708rad)
FEATURE [App::Part] Part  label="Foot"
  Group = -> [Body,nut,base]
  Origin = -> Origin
---- part ../Part/Print/LinePower_Cover.FCStd = doc fcstd_72adacda487f ----
FCSTD DOCUMENT  (FreeCAD 1.0R39319 (Git))
Label: LinePower_Cover
License: All rights reserved
LicenseURL: https://en.wikipedia.org/wiki/All_rights_reserved
objects: Sketcher::SketchObject×12, PartDesign::Pocket×9, PartDesign::Fillet×8, PartDesign::Pad×3, PartDesign::Body×1, PartDesign::CoordinateSystem×1, App::Part×1
note: 86 computed .brp shape members not serialized (recipe doc carries the construction recipe); baked Part::Feature solids carry a one-line shape summary decoded from their .brp

FEATURE [Sketcher::SketchObject] Sketch
  ArcFitTolerance = 1e-06
  AttachmentSupport = -> [XY_Plane001]
  FullyConstrained = true
  MakeInternals = false
  MapMode = 5
  sketch-geometry (4):
    g0: LineSegment StartX=0 StartY=0 StartZ=0 EndX=49 EndY=0 EndZ=0
    g1: LineSegment StartX=49 StartY=0 StartZ=0 EndX=49 EndY=40 EndZ=0
    g2: LineSegment StartX=49 StartY=40 StartZ=0 EndX=0 EndY=40 EndZ=0
    g3: LineSegment StartX=0 StartY=40 StartZ=0 EndX=0 EndY=0 EndZ=0
  constraints (11):
    c: Coincident(g0,g1)
    c: Coincident(g1,g2)
    c: Coincident(g2,g3)
    c: Coincident(g3,g0)
    c: Horizontal(g0)
    c: Horizontal(g2)
    c: Vertical(g1)
    c: Vertical(g3)
    c: Coincident(g0,g-1)
    c: Distance(g0,g2) = 40
    c: Distance(g1,g3) = 49
FEATURE [PartDesign::Pad] Pad
  Direction = (0,0,1)
  Length = 33
  Length2 = 10
  Profile = -> Sketch
  ReferenceAxis = -> Sketch [N_Axis]
  Refine = true
  Suppressed = false
  Type = 0
FEATURE [Sketcher::SketchObject] Sketch001
  ArcFitTolerance = 1e-06
  AttachmentSupport = -> [XY_Plane001]
  ExternalGeometry = -> [Pad]
  FullyConstrained = true
  MakeInternals = false
  MapMode = 5
  sketch-geometry (4):
    g0: LineSegment StartX=0 StartY=0 StartZ=0 EndX=47 EndY=0 EndZ=0
    g1: LineSegment StartX=47 StartY=0 StartZ=0 EndX=47 EndY=21 EndZ=0
    g2: LineSegment StartX=47 StartY=21 StartZ=0 EndX=0 EndY=21 EndZ=0
    g3: LineSegment StartX=0 StartY=21 StartZ=0 EndX=0 EndY=0 EndZ=0
  constraints (11):
    c: Coincident(g0,g1)
    c: Coincident(g1,g2)
    c: Coincident(g2,g3)
    c: Coincident(g3,g0)
    c: Horizontal(g0)
    c: Horizontal(g2)
    c: Vertical(g1)
    c: Vertical(g3)
    c: Coincident(g0,g-1)
    c: Distance(g0,g2) = 21
    c: Distance(g-3,g1) = 2
FEATURE [PartDesign::Pocket] Pocket
  BaseFeature = -> Pad
  Direction = (0,0,-1)
  Length = 31
  Length2 = 5
  Profile = -> Sketch001
  ReferenceAxis = -> Sketch001 [N_Axis]
  Refine = true
  Reversed = true
  Suppressed = false
  Type = 0
FEATURE [Sketcher::SketchObject] Sketch002
  ArcFitTolerance = 1e-06
  AttachmentSupport = -> [Pocket]
  ExternalGeometry = -> [Pocket]
  FullyConstrained = true
  MakeInternals = false
  MapMode = 5
  Placement = pos=(0,0,0) rot=(1,0,0;3.14159rad)
  sketch-geometry (4):
    g0: LineSegment StartX=7 StartY=-40 StartZ=0 EndX=49 EndY=-40 EndZ=0
    g1: LineSegment StartX=49 StartY=-40 StartZ=0 EndX=49 EndY=-21 EndZ=0
    g2: LineSegment StartX=49 StartY=-21 StartZ=0 EndX=7 EndY=-21 EndZ=0
    g3: LineSegment StartX=7 StartY=-21 StartZ=0 EndX=7 EndY=-40 EndZ=0
  constraints (12):
    c: Coincident(g0,g1)
    c: Coincident(g1,g2)
    c: Coincident(g2,g3)
    c: Coincident(g3,g0)
    c: Horizontal(g0)
    c: Horizontal(g2)
    c: Vertical(g1)
    c: Vertical(g3)
    c: PointOnObject(g0,g-4)
    c: PointOnObject(g-3,g2)
    c: Distance(g3,g-2) = 7
    c: PointOnObject(g-5,g1)
FEATURE [PartDesign::Pocket] Pocket001
  BaseFeature = -> Pocket
  Direction = (0,0,1)
  Length = 31
  Length2 = 5
  Profile = -> Sketch002
  ReferenceAxis = -> Sketch002 [N_Axis]
  Refine = true
  Suppressed = false
  Type = 0
FEATURE [Sketcher::SketchObject] Sketch003
  ArcFitTolerance = 1e-06
  AttachmentSupport = -> [Pocket001]
  ExternalGeometry = -> [Pocket001]
  FullyConstrained = true
  MakeInternals = false
  MapMode = 5
  Placement = pos=(0,0,0) rot=(1,0,0;3.14159rad)
  sketch-geometry (4):
    g0: LineSegment StartX=7 StartY=-21 StartZ=0 EndX=0 EndY=-21 EndZ=0
    g1: LineSegment StartX=0 StartY=-21 StartZ=0 EndX=0 EndY=-28 EndZ=0
    g2: LineSegment StartX=0 StartY=-28 StartZ=0 EndX=7 EndY=-28 EndZ=0
    g3: LineSegment StartX=7 StartY=-28 StartZ=0 EndX=7 EndY=-21 EndZ=0
  constraints (11):
    c: Coincident(g0,g1)
    c: Coincident(g1,g2)
    c: Coincident(g2,g3)
    c: Coincident(g3,g0)
    c: Horizontal(g0)
    c: Horizontal(g2)
    c: Vertical(g1)
    c: Vertical(g3)
    c: Coincident(g0,g-4)
    c: PointOnObject(g1,g-2)
    c: Distance(g-1,g2) = 28
FEATURE [PartDesign::Pocket] Pocket002
  BaseFeature = -> Pocket001
  Direction = (0,0,1)
  Length = 31
  Length2 = 5
  Profile = -> Sketch003
  ReferenceAxis = -> Sketch003 [N_Axis]
  Refine = true
  Suppressed = false
  Type = 0
FEATURE [Sketcher::SketchObject] Sketch004
  ArcFitTolerance = 1e-06
  AttachmentSupport = -> [Pocket002]
  ExternalGeometry = -> [Pocket002]
  FullyConstrained = true
  MakeInternals = false
  MapMode = 5
  Placement = pos=(0,0,31) rot=(1,0,0;3.14159rad)
  sketch-geometry (4):
    g0: LineSegment StartX=47 StartY=0 StartZ=0 EndX=37 EndY=0 EndZ=0
    g1: LineSegment StartX=37 StartY=0 StartZ=0 EndX=37 EndY=-10 EndZ=0
    g2: LineSegment StartX=37 StartY=-10 StartZ=0 EndX=47 EndY=-10 EndZ=0
    g3: LineSegment StartX=47 StartY=-10 StartZ=0 EndX=47 EndY=0 EndZ=0
  constraints (11):
    c: Coincident(g0,g1)
    c: Coincident(g1,g2)
    c: Coincident(g2,g3)
    c: Coincident(g3,g0)
    c: Horizontal(g0)
    c: Horizontal(g2)
    c: Vertical(g1)
    c: Vertical(g3)
    c: Coincident(g0,g-3)
    c: Distance(g0,g2) = 10
    c: Distance(g3,g1) = 10
FEATURE [PartDesign::Pad] Pad001
  BaseFeature = -> Pocket002
  Direction = (0,0,-1)
  Length = 27
  Length2 = 10
  Profile = -> Sketch004
  ReferenceAxis = -> Sketch004 [N_Axis]
  Refine = true
  Suppressed = false
  Type = 0
FEATURE [Sketcher::SketchObject] Sketch005
  ArcFitTolerance = 1e-06
  AttachmentSupport = -> [Pad001]
  ExternalGeometry = -> [Pad001]
  FullyConstrained = true
  MakeInternals = false
  MapMode = 5
  Placement = pos=(0,0,33) rot=(0,0,1;0rad)
  sketch-geometry (4):
    g0: LineSegment StartX=49 StartY=0 StartZ=0 EndX=49 EndY=8 EndZ=0
    g1: LineSegment StartX=49 StartY=8 StartZ=0 EndX=39 EndY=8 EndZ=0
    g2: LineSegment StartX=39 StartY=8 StartZ=0 EndX=39 EndY=0 EndZ=0
    g3: LineSegment StartX=39 StartY=0 StartZ=0 EndX=49 EndY=0 EndZ=0
  constraints (11):
    c: Coincident(g0,g1)
    c: Coincident(g1,g2)
    c: Coincident(g2,g3)
    c: Coincident(g3,g0)
    c: Vertical(g0)
    c: Vertical(g2)
    c: Horizontal(g1)
    c: Horizontal(g3)
    c: Coincident(g0,g-3)
    c: Distance(g-5,g1) = 2
    c: Distance(g-4,g2) = 2
FEATURE [PartDesign::Pocket] Pocket003
  BaseFeature = -> Pad001
  Direction = (0,0,-1)
  Length = 0
  Length2 = 5
  Offset = -2
  Profile = -> Sketch005
  ReferenceAxis = -> Sketch005 [N_Axis]
  Refine = true
  Suppressed = false
  Type = 3
  UpToFace = -> Pad001 [Face14]
FEATURE [Sketcher::SketchObject] Sketch006
  ArcFitTolerance = 1e-06
  AttachmentSupport = -> [Pocket003]
  ExternalGeometry = -> [Pocket003]
  FullyConstrained = true
  MakeInternals = false
  MapMode = 5
  Placement = pos=(0,0,0) rot=(1,0,0;3.14159rad)
  sketch-geometry (4):
    g0: LineSegment StartX=7 StartY=-28 StartZ=0 EndX=0 EndY=-28 EndZ=0
    g1: LineSegment StartX=0 StartY=-28 StartZ=0 EndX=0 EndY=-40 EndZ=0
    g2: LineSegment StartX=0 StartY=-40 StartZ=0 EndX=7 EndY=-40 EndZ=0
    g3: LineSegment StartX=7 StartY=-40 StartZ=0 EndX=7 EndY=-28 EndZ=0
  constraints (10):
    c: Coincident(g0,g1)
    c: Coincident(g1,g2)
    c: Coincident(g2,g3)
    c: Coincident(g3,g0)
    c: Horizontal(g0)
    c: Horizontal(g2)
    c: Vertical(g1)
    c: Vertical(g3)
    c: Coincident(g0,g-4)
    c: Coincident(g1,g-5)
FEATURE [PartDesign::Pocket] Pocket004
  BaseFeature = -> Pocket003
  Direction = (0,0,1)
  Length = 0
  Length2 = 5
  Profile = -> Sketch006
  ReferenceAxis = -> Sketch006 [N_Axis]
  Refine = true
  Suppressed = false
  Type = 3
  UpToFace = -> Pocket003 [Face18]
FEATURE [Sketcher::SketchObject] Sketch007
  ArcFitTolerance = 1e-06
  AttachmentSupport = -> [Pocket004]
  ExternalGeometry = -> [Pocket004]
  FullyConstrained = true
  MakeInternals = false
  MapMode = 5
  Placement = pos=(0,0,33) rot=(0,0,1;0rad)
  sketch-geometry (4):
    g0: LineSegment StartX=0 StartY=40 StartZ=0 EndX=0 EndY=30 EndZ=0
    g1: LineSegment StartX=0 StartY=30 StartZ=0 EndX=5 EndY=30 EndZ=0
    g2: LineSegment StartX=5 StartY=30 StartZ=0 EndX=5 EndY=40 EndZ=0
    g3: LineSegment StartX=5 StartY=40 StartZ=0 EndX=0 EndY=40 EndZ=0
  constraints (11):
    c: Coincident(g0,g1)
    c: Coincident(g1,g2)
    c: Coincident(g2,g3)
    c: Coincident(g3,g0)
    c: Vertical(g0)
    c: Vertical(g2)
    c: Horizontal(g1)
    c: Horizontal(g3)
    c: Coincident(g0,g-3)
    c: Distance(g-5,g2) = 2
    c: Distance(g-4,g1) = 2
FEATURE [PartDesign::Pocket] Pocket005
  BaseFeature = -> Pocket004
  Direction = (0,0,-1)
  Length = 0
  Length2 = 5
  Offset = -2
  Profile = -> Sketch007
  ReferenceAxis = -> Sketch007 [N_Axis]
  Refine = true
  Suppressed = false
  Type = 3
  UpToFace = -> Pocket004 [Face2]
FEATURE [PartDesign::Fillet] Fillet
  Base = -> Pocket005 [Edge55]
  BaseFeature = -> Pocket005
  Radius = 4
  Refine = true
  SupportTransform = false
  Suppressed = false
  UseAllEdges = false
FEATURE [Sketcher::SketchObject] Sketch008
  ArcFitTolerance = 1e-06
  AttachmentSupport = -> [Fillet]
  ExternalGeometry = -> [Fillet]
  FullyConstrained = true
  MakeInternals = false
  MapMode = 5
  Placement = pos=(0,0,6) rot=(0,0,1;0rad)
  sketch-geometry (1):
    g0: Circle CenterX=43 CenterY=4 CenterZ=0 NormalX=0 NormalY=0 NormalZ=1 AngleXU=0 Radius=1.6
  constraints (3):
    c: Diameter(g0) = 3.2
    c: Distance(g0,g-4) = 4
    c: Distance(g0,g-3) = 4
FEATURE [PartDesign::Pocket] Pocket006
  BaseFeature = -> Fillet
  Direction = (0,0,-1)
  Length = 5
  Length2 = 5
  Profile = -> Sketch008
  ReferenceAxis = -> Sketch008 [N_Axis]
  Refine = true
  Suppressed = false
  Type = 1
FEATURE [Sketcher::SketchObject] Sketch009
  ArcFitTolerance = 1e-06
  AttachmentSupport = -> [Pocket006]
  FullyConstrained = true
  MakeInternals = false
  MapMode = 5
  Placement = pos=(0,0,6) rot=(0,0,1;0rad)
  sketch-geometry (1):
    g0: Circle CenterX=3 CenterY=36 CenterZ=0 NormalX=0 NormalY=0 NormalZ=1 AngleXU=0 Radius=1.6
  constraints (3):
    c: Diameter(g0) = 3.2
    c: DistanceY(g-1,g0) = 36
    c: Distance(g0,g-2) = 3
FEATURE [PartDesign::Pocket] Pocket007
  BaseFeature = -> Pocket006
  Direction = (0,0,-1)
  Length = 5
  Length2 = 5
  Profile = -> Sketch009
  ReferenceAxis = -> Sketch009 [N_Axis]
  Refine = true
  Suppressed = false
  Type = 1
FEATURE [Sketcher::SketchObject] Sketch010
  ArcFitTolerance = 1e-06
  AttachmentSupport = -> [Pocket007]
  ExternalGeometry = -> [Pocket007]
  FullyConstrained = true
  MakeInternals = false
  MapMode = 5
  Placement = pos=(0,0,33) rot=(0,0,1;0rad)
  sketch-geometry (1):
    g0: Circle CenterX=3 CenterY=36 CenterZ=0 NormalX=0 NormalY=0 NormalZ=1 AngleXU=0 Radius=2.75
  constraints (2):
    c: Coincident(g0,g-3)
    c: Diameter(g0) = 5.5
FEATURE [PartDesign::Pocket] Pocket008
  BaseFeature = -> Pocket007
  Direction = (0,0,-1)
  Length = 0
  Length2 = 5
  Profile = -> Sketch010
  ReferenceAxis = -> Sketch010 [N_Axis]
  Refine = true
  Suppressed = false
  Type = 3
  UpToFace = -> Pocket007 [Face16]
FEATURE [PartDesign::Fillet] Fillet001
  Base = -> Pocket008 [Edge32]
  BaseFeature = -> Pocket008
  Radius = 2
  Refine = true
  SupportTransform = false
  Suppressed = false
  UseAllEdges = false
FEATURE [PartDesign::Fillet] Fillet002
  Base = -> Fillet001 [Edge44]
  BaseFeature = -> Fillet001
  Radius = 4
  Refine = true
  SupportTransform = false
  Suppressed = false
  UseAllEdges = false
FEATURE [Sketcher::SketchObject] Sketch011
  ArcFitTolerance = 1e-06
  AttachmentSupport = -> [Fillet002]
  ExternalGeometry = -> [Fillet002]
  FullyConstrained = true
  MakeInternals = false
  MapMode = 5
  Placement = pos=(49,0,0) rot=(0.57735,0.57735,0.57735;2.0944rad)
  sketch-geometry (4):
    g0: LineSegment StartX=21 StartY=31 StartZ=0 EndX=21 EndY=22.5 EndZ=0
    g1: LineSegment StartX=21 StartY=22.5 StartZ=0 EndX=32.5 EndY=22.5 EndZ=0
    g2: LineSegment StartX=32.5 StartY=22.5 StartZ=0 EndX=32.5 EndY=31 EndZ=0
    g3: LineSegment StartX=32.5 StartY=31 StartZ=0 EndX=21 EndY=31 EndZ=0
  constraints (11):
    c: Coincident(g0,g1)
    c: Coincident(g1,g2)
    c: Coincident(g2,g3)
    c: Coincident(g3,g0)
    c: Vertical(g0)
    c: Vertical(g2)
    c: Horizontal(g1)
    c: Horizontal(g3)
    c: Coincident(g0,g-4)
    c: Distance(g2,g0) = 11.5
    c: Distance(g1,g-1) = 22.5
FEATURE [PartDesign::Pad] Pad002
  BaseFeature = -> Fillet002
  Direction = (1,0,0)
  Length = 10
  Length2 = 10
  Profile = -> Sketch011
  ReferenceAxis = -> Sketch011 [N_Axis]
  Refine = true
  Suppressed = false
  Type = 3
  UpToFace = -> Fillet002 [Face22]
FEATURE [PartDesign::Fillet] Fillet003
  Base = -> Pad002 [Edge3,Edge65]
  BaseFeature = -> Pad002
  Radius = 2
  Refine = true
  SupportTransform = false
  Suppressed = false
  UseAllEdges = false
FEATURE [PartDesign::Fillet] Fillet004
  Base = -> Fillet003 [Edge72]
  BaseFeature = -> Fillet003
  Radius = 4
  Refine = true
  SupportTransform = false
  Suppressed = false
  UseAllEdges = false
FEATURE [PartDesign::Fillet] Fillet005
  Base = -> Fillet004 [Edge57]
  BaseFeature = -> Fillet004
  Radius = 6
  Refine = true
  SupportTransform = false
  Suppressed = false
  UseAllEdges = false
FEATURE [PartDesign::Fillet] Fillet006
  Base = -> Fillet005 [Edge27]
  BaseFeature = -> Fillet005
  Radius = 2
  Refine = true
  SupportTransform = false
  Suppressed = false
  UseAllEdges = false
FEATURE [PartDesign::Fillet] Fillet007
  Base = -> Fillet006 [Edge33]
  BaseFeature = -> Fillet006
  Radius = 2
  Refine = true
  SupportTransform = false
  Suppressed = false
  UseAllEdges = false
FEATURE [PartDesign::Body] Body  label="LinePower_Cover001"
  AllowCompound = false
  Group = -> [Sketch,Pad,Sketch001,Pocket,Sketch002,Pocket001,Sketch003,Pocket002,Sketch004,Pad001,Sketch005,Pocket003,Sketch006,Pocket004,Sketch007,Pocket005,Fillet,Sketch008,Pocket006,Sketch009,Pocket007,Sketch010,Pocket008,Fillet001,Fillet002,Sketch011,Pad002,Fillet003,Fillet004,Fillet005,Fillet006,Fillet007]
  Origin = -> Origin001
  Tip = -> Fillet007
FEATURE [PartDesign::CoordinateSystem] stack_att
  AttacherType = Attacher::AttachEngine3D
  AttachmentSupport = -> [Fillet007]
  MapMode = 11
  Placement = pos=(43,4,4) rot=(0,0,1;1.5708rad)
FEATURE [App::Part] Part  label="LinePower_Cover"
  Group = -> [Body,stack_att]
  Origin = -> Origin
---- part ../Part/Print/Spacer.FCStd = doc fcstd_2f39e15fa6d1 ----
FCSTD DOCUMENT  (FreeCAD 1.0R39319 (Git))
Label: Spacer
License: All rights reserved
LicenseURL: https://en.wikipedia.org/wiki/All_rights_reserved
objects: Sketcher::SketchObject×1, PartDesign::Pad×1, PartDesign::Chamfer×1, PartDesign::Body×1, PartDesign::CoordinateSystem×1, App::Part×1
note: 10 computed .brp shape members not serialized (recipe doc carries the construction recipe); baked Part::Feature solids carry a one-line shape summary decoded from their .brp

FEATURE [Sketcher::SketchObject] Sketch
  ArcFitTolerance = 1e-06
  AttachmentSupport = -> [XY_Plane001]
  FullyConstrained = true
  MakeInternals = false
  MapMode = 5
  sketch-geometry (2):
    g0: Circle CenterX=0 CenterY=0 CenterZ=0 NormalX=0 NormalY=0 NormalZ=1 AngleXU=0 Radius=4.25
    g1: Circle CenterX=0 CenterY=0 CenterZ=0 NormalX=0 NormalY=0 NormalZ=1 AngleXU=0 Radius=3.25
  constraints (4):
    c: Coincident(g0,g-1)
    c: Coincident(g1,g0)
    c: Diameter(g1) = 6.5
    c: Diameter(g0) = 8.5
FEATURE [PartDesign::Pad] Pad
  Direction = (0,0,1)
  Length = 7
  Length2 = 10
  Profile = -> Sketch
  ReferenceAxis = -> Sketch [N_Axis]
  Refine = true
  Suppressed = false
  Type = 0
FEATURE [PartDesign::Chamfer] Chamfer
  Angle = 45
  Base = -> Pad [Edge3,Edge2]
  BaseFeature = -> Pad
  ChamferType = 0
  FlipDirection = false
  Refine = true
  Size = 0.25
  Size2 = 1
  SupportTransform = false
  Suppressed = false
  UseAllEdges = false
FEATURE [PartDesign::Body] Body  label="Spacer001"
  AllowCompound = false
  Group = -> [Sketch,Pad,Chamfer]
  Origin = -> Origin001
  Tip = -> Chamfer
FEATURE [PartDesign::CoordinateSystem] LCS_1
  AttacherType = Attacher::AttachEngine3D
  AttachmentSupport = -> [Chamfer]
  MapMode = 11
  Placement = pos=(0,0,0) rot=(0,0,1;1.5708rad)
FEATURE [App::Part] Part  label="Spacer"
  Group = -> [Body,LCS_1]
  Origin = -> Origin
